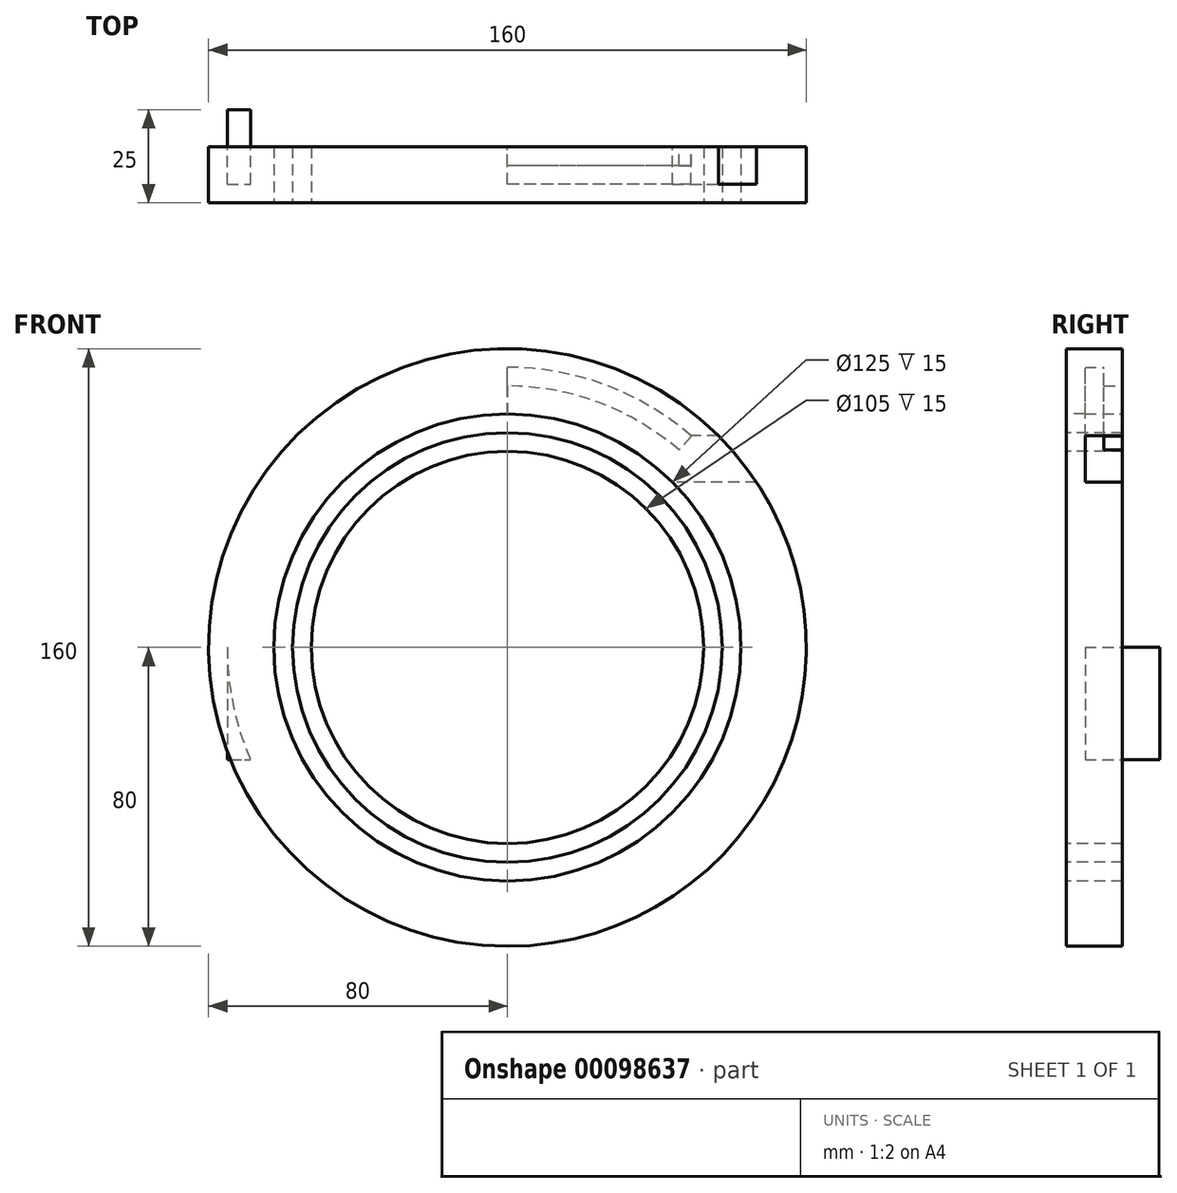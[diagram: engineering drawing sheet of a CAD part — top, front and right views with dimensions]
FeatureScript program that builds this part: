
annotation { "Feature Type Name" : "Feature", "Feature Type Description" : "" }
export const myFeature = defineFeature(function(context is Context, id is Id, definition is map)
    precondition{}
    {
        {
            var Q0;
            Q0=qCreatedBy(makeId("Front.planeOp"),FACE);
            var sketch = newSketch(context, id + "F0", { "sketchPlane" : qUnion([Q0])});
            skCircle(sketch, "E0", {"center": v(0, 0) * mm, "radius": 62.5 * mm});
            skCircle(sketch, "E1", {"center": v(0, 0) * mm, "radius": 75 * mm});
            skLineSegment(sketch, "E2", {"start": v(-62.5, 0) * mm, "end": v(-75, 0) * mm});
            skLineSegment(sketch, "E3", {"start": v(0, 0) * mm, "end": v(53.03, 53.03) * mm});
            skLineSegment(sketch, "E4.bottom", {"start": v(-75, 0) * mm, "end": v(-62.5, 0) * mm});
            skLineSegment(sketch, "E4.top", {"start": v(-75, -30) * mm, "end": v(-62.5, -30) * mm});
            skLineSegment(sketch, "E4.left", {"start": v(-75, 0) * mm, "end": v(-75, -30) * mm});
            skLineSegment(sketch, "E4.right", {"start": v(-62.5, 0) * mm, "end": v(-62.5, -30) * mm});
            skLineSegment(sketch, "E5.left", {"start": v(0, 62.5) * mm, "end": v(0, 75) * mm});
            skLineSegment(sketch, "E6.bottom", {"start": v(44.2, 44.2) * mm, "end": v(79.2, 44.2) * mm});
            skLineSegment(sketch, "E6.top", {"start": v(44.2, 56.7) * mm, "end": v(79.2, 56.7) * mm});
            skLineSegment(sketch, "E6.left", {"start": v(44.2, 44.2) * mm, "end": v(44.2, 56.7) * mm});
            skLineSegment(sketch, "E6.right", {"start": v(79.2, 44.2) * mm, "end": v(79.2, 56.7) * mm});
            skSolve(sketch);
        }
        {
            var Q0;
            {var subQ0=sQuery(id+"F0.wireOp",EDGE,"E4.bottom");Q0=makeQuery(id+"F0.imprint","IMPRINT",FACE,{"disambiguationData":[TD([[makeQuery(id+"F0.imprint","IMPRINT",EDGE,{"derivedFrom":subQ0}),-1.0]])]});}
            var Q1;
            {var subQ0=sQuery(id+"F0.wireOp",EDGE,"E4.left");Q1=makeQuery(id+"F0.imprint","IMPRINT",FACE,{"disambiguationData":[TD([[makeQuery(id+"F0.imprint","IMPRINT",EDGE,{"derivedFrom":subQ0}),1.0]])]});}
            var Q2;
            {var subQ0=sQuery(id+"F0.wireOp",EDGE,"E4.bottom");Q2=makeQuery(id+"F0.imprint","IMPRINT",FACE,{"disambiguationData":[TD([[makeQuery(id+"F0.imprint","IMPRINT",EDGE,{"derivedFrom":subQ0}),1.0]])]});}
            var Q3;
            {var subQ0=sQuery(id+"F0.wireOp",EDGE,"E5.left");Q3=makeQuery(id+"F0.imprint","IMPRINT",FACE,{"disambiguationData":[TD([[makeQuery(id+"F0.imprint","IMPRINT",EDGE,{"derivedFrom":subQ0}),-1.0]])]});}
            var Q4;
            {var subQ3=sQuery(id+"F0.wireOp",EDGE,"E3");var subQ5=sQuery(id+"F0.wireOp",EDGE,"E1");var subQ6=makeQuery(id+"F0.imprint","INTERSECT",VERTEX,{"derivedFrom":[subQ5,subQ3]});Q4=makeQuery(id+"F0.imprint","IMPRINT",FACE,{"disambiguationData":[TD([[makeQuery(id+"F0.imprint","IMPRINT",EDGE,{"disambiguationData":[TD([[subQ6,-1.0]])],"derivedFrom":subQ5}),1.0]])]});}
            var Q5;
            {var subQ0=sQuery(id+"F0.wireOp",EDGE,"E5.top");Q5=makeQuery(id+"F0.imprint","IMPRINT",FACE,{"disambiguationData":[TD([[makeQuery(id+"F0.imprint","IMPRINT",EDGE,{"derivedFrom":subQ0}),-1.0]])]});}
            var Q6;
            {var subQ0=sQuery(id+"F0.wireOp",EDGE,"E6.right");Q6=makeQuery(id+"F0.imprint","IMPRINT",FACE,{"disambiguationData":[TD([[makeQuery(id+"F0.imprint","IMPRINT",EDGE,{"derivedFrom":subQ0}),1.0]])]});}
            var Q7;
            {var subQ0=sQuery(id+"F0.wireOp",EDGE,"E3");var subQ1=sQuery(id+"F0.wireOp",EDGE,"E1");var subQ2=makeQuery(id+"F0.imprint","INTERSECT",VERTEX,{"derivedFrom":[subQ1,subQ0]});Q7=makeQuery(id+"F0.imprint","IMPRINT",FACE,{"disambiguationData":[TD([[makeQuery(id+"F0.imprint","IMPRINT",EDGE,{"disambiguationData":[TD([[subQ2,1.0]])],"derivedFrom":subQ1}),1.0]])]});}
            extrude(context, id + "F1", {"entities" : qUnion([Q0, Q1, Q2, Q3, Q4, Q5, Q6, Q7]), "endBound" : BoundingType.SYMMETRIC, "depth" : 20 * mm});
        }
        {
            var Q0;
            Q0=qCreatedBy(makeId("Front.planeOp"),FACE);
            var sketch = newSketch(context, id + "F2", { "sketchPlane" : qUnion([Q0])});
            skCircle(sketch, "E7", {"center": v(0, 0) * mm, "radius": 75 * mm});
            skCircle(sketch, "E8", {"center": v(0, 0) * mm, "radius": 70 * mm});
            skLineSegment(sketch, "E9", {"start": v(0, 0) * mm, "end": v(49.2, 56.6) * mm});
            skLineSegment(sketch, "E10", {"start": v(0, 0) * mm, "end": v(-75, 0) * mm});
            skSolve(sketch);
        }
        {
            var Q0;
            {var subQ0=sQuery(id+"F2.wireOp",EDGE,"E9");var subQ1=sQuery(id+"F2.wireOp",EDGE,"E7");var subQ2=makeQuery(id+"F2.imprint","INTERSECT",VERTEX,{"derivedFrom":[subQ1,subQ0]});Q0=makeQuery(id+"F2.imprint","IMPRINT",FACE,{"disambiguationData":[TD([[makeQuery(id+"F2.imprint","IMPRINT",EDGE,{"disambiguationData":[TD([[subQ2,-1.0]])],"derivedFrom":subQ1}),1.0]])]});}
            extrude(context, id + "F3", {"entities" : qUnion([Q0]), "operationType" : NewBodyOperationType.REMOVE, "endBound" : BoundingType.SYMMETRIC, "depth" : 10 * mm});
        }
        {
            var Q0;
            Q0=qCreatedBy(makeId("Front.planeOp"),FACE);
            var sketch = newSketch(context, id + "F4", { "sketchPlane" : qUnion([Q0])});
            skCircle(sketch, "E11", {"center": v(0, 0) * mm, "radius": 57.5 * mm});
            skCircle(sketch, "E12", {"center": v(0, 0) * mm, "radius": 80 * mm});
            skLineSegment(sketch, "E13", {"start": v(0, 0) * mm, "end": v(0, 80) * mm});
            skLineSegment(sketch, "E14", {"start": v(0, 80) * mm, "end": v(0, 0) * mm});
            skLineSegment(sketch, "E15", {"start": v(0, 0) * mm, "end": v(-78.78, 13.9) * mm});
            skSolve(sketch);
        }
        {
            var Q0;
            {var subQ0=sQuery(id+"F4.wireOp",EDGE,"E14");var subQ1=sQuery(id+"F4.wireOp",EDGE,"E11");var subQ2=makeQuery(id+"F4.imprint","INTERSECT",VERTEX,{"derivedFrom":[subQ1,subQ0]});Q0=makeQuery(id+"F4.imprint","IMPRINT",FACE,{"disambiguationData":[TD([[makeQuery(id+"F4.imprint","IMPRINT",EDGE,{"disambiguationData":[TD([[subQ2,-1.0]])],"derivedFrom":subQ1}),-1.0]])]});}
            extrude(context, id + "F5", {"entities" : qUnion([Q0]), "depth" : 15 * mm});
        }
        {
            var Q0;
            Q0=makeQuery(id+"F1.opExtrude","SWEPT_BODY",BODY,{"disambiguationData":[OSD([sQuery(id+"F0.wireOp",EDGE,"E0"),sQuery(id+"F0.wireOp",EDGE,"E1"),sQuery(id+"F0.wireOp",EDGE,"E4.top"),sQuery(id+"F0.wireOp",EDGE,"E4.left"),sQuery(id+"F0.wireOp",EDGE,"E4.right"),sQuery(id+"F0.wireOp",EDGE,"E6.bottom"),sQuery(id+"F0.wireOp",EDGE,"E6.top"),sQuery(id+"F0.wireOp",EDGE,"E6.right")])]});
            var Q1;
            Q1=makeQuery(id+"F5.opExtrude","SWEPT_BODY",BODY,{"disambiguationData":[OSD([sQuery(id+"F4.wireOp",EDGE,"E11"),sQuery(id+"F4.wireOp",EDGE,"E12"),sQuery(id+"F4.wireOp",EDGE,"E14"),sQuery(id+"F4.wireOp",EDGE,"E15")])]});
            booleanBodies(context, id + "F6", {"operationType" : BooleanOperationType.SUBTRACTION, "tools" : qUnion([Q0]), "targets" : qUnion([Q1])});
        }
        {
            var Q0;
            Q0=makeQuery(id+"F5.opExtrude","CAP_FACE",FACE,{"disambiguationData":[OSD([sQuery(id+"F4.wireOp",EDGE,"E11"),sQuery(id+"F4.wireOp",EDGE,"E12"),sQuery(id+"F4.wireOp",EDGE,"E14"),sQuery(id+"F4.wireOp",EDGE,"E15")])],"isStart":false});
            var sketch = newSketch(context, id + "F7", { "sketchPlane" : qUnion([Q0])});
            skCircle(sketch, "E16", {"center": v(0, 0) * mm, "radius": 57.5 * mm});
            skCircle(sketch, "E17", {"center": v(0, 0) * mm, "radius": 52.5 * mm});
            skCircle(sketch, "E18", {"center": v(0, 0) * mm, "radius": 62.5 * mm});
            skLineSegment(sketch, "E19", {"start": v(0, 0) * mm, "end": v(-69.28, 40) * mm});
            skLineSegment(sketch, "E20", {"start": v(-69.28, 40) * mm, "end": v(0, 0) * mm});
            skLineSegment(sketch, "E21", {"start": v(0, 0) * mm, "end": v(-27.36, 75.18) * mm});
            skLineSegment(sketch, "E22", {"start": v(0, 0) * mm, "end": v(-17.23, 60.08) * mm});
            skLineSegment(sketch, "E23", {"start": v(-17.23, 60.08) * mm, "end": v(0, 0) * mm});
            skLineSegment(sketch, "E24", {"start": v(0, 0) * mm, "end": v(-12.34, 61.27) * mm});
            skLineSegment(sketch, "E25", {"start": v(-12.34, 61.27) * mm, "end": v(0, 0) * mm});
            skLineSegment(sketch, "E26", {"start": v(0, 0) * mm, "end": v(-8.04, 61.98) * mm});
            skLineSegment(sketch, "E27", {"start": v(-8.04, 61.98) * mm, "end": v(0, 0) * mm});
            skLineSegment(sketch, "E28", {"start": v(0, 0) * mm, "end": v(-51.51, 35.4) * mm});
            skLineSegment(sketch, "E29", {"start": v(-51.51, 35.4) * mm, "end": v(0, 0) * mm});
            skLineSegment(sketch, "E30", {"start": v(-48.92, 38.9) * mm, "end": v(0, 0) * mm});
            skLineSegment(sketch, "E31", {"start": v(-46.08, 42.22) * mm, "end": v(0, 0) * mm});
            skLineSegment(sketch, "E32", {"start": v(0, 0) * mm, "end": v(0, 0) * mm});
            skSolve(sketch);
        }
        {
            var Q0;
            {var subQ0=sQuery(id+"F7.wireOp",EDGE,"E29");var subQ1=sQuery(id+"F7.wireOp",EDGE,"E16");var subQ2=makeQuery(id+"F7.imprint","INTERSECT",VERTEX,{"derivedFrom":[subQ1,subQ0]});Q0=makeQuery(id+"F7.imprint","IMPRINT",FACE,{"disambiguationData":[TD([[makeQuery(id+"F7.imprint","IMPRINT",EDGE,{"disambiguationData":[TD([[subQ2,-1.0]])],"derivedFrom":subQ1}),1.0]])]});}
            var Q1;
            {var subQ0=sQuery(id+"F7.wireOp",EDGE,"E23");var subQ1=sQuery(id+"F7.wireOp",EDGE,"E16");var subQ2=makeQuery(id+"F7.imprint","INTERSECT",VERTEX,{"derivedFrom":[subQ1,subQ0]});Q1=makeQuery(id+"F7.imprint","IMPRINT",FACE,{"disambiguationData":[TD([[makeQuery(id+"F7.imprint","IMPRINT",EDGE,{"disambiguationData":[TD([[subQ2,-1.0]])],"derivedFrom":subQ1}),1.0]])]});}
            var Q2;
            {var subQ0=sQuery(id+"F4.wireOp",EDGE,"E11");var subQ1=sQuery(id+"F4.wireOp",EDGE,"E14");var subQ2=sQuery(id+"F4.wireOp",EDGE,"E15");Q2=makeQuery(id+"F6.opBoolean","SPLIT",FACE,{"disambiguationData":[TD([makeQuery(id+"F1.opExtrude","SWEPT_FACE",FACE,{"disambiguationData":[OSD([sQuery(id+"F0.wireOp",EDGE,"E0")])]})])],"derivedFrom":makeQuery(id+"F5.opExtrude","CAP_FACE",FACE,{"disambiguationData":[OSD([subQ0,sQuery(id+"F4.wireOp",EDGE,"E12"),subQ1,subQ2])],"isStart":true})});}
            extrude(context, id + "F8", {"entities" : qUnion([Q0, Q1]), "operationType" : NewBodyOperationType.ADD, "endBound" : BoundingType.UP_TO_SURFACE, "oppositeDirection" : true, "endBoundEntityFace" : qUnion([Q2]), "depth" : 25 * mm});
        }
        {
            var Q0;
            {var subQ0=sQuery(id+"F7.wireOp",EDGE,"E31");var subQ1=sQuery(id+"F7.wireOp",EDGE,"E16");var subQ2=makeQuery(id+"F7.imprint","INTERSECT",VERTEX,{"derivedFrom":[subQ1,subQ0]});Q0=makeQuery(id+"F7.imprint","IMPRINT",FACE,{"disambiguationData":[TD([[makeQuery(id+"F7.imprint","IMPRINT",EDGE,{"disambiguationData":[TD([[subQ2,-1.0]])],"derivedFrom":subQ1}),-1.0]])]});}
            var Q1;
            {var subQ0=sQuery(id+"F7.wireOp",EDGE,"E27");var subQ1=sQuery(id+"F7.wireOp",EDGE,"E16");var subQ2=makeQuery(id+"F7.imprint","INTERSECT",VERTEX,{"derivedFrom":[subQ1,subQ0]});Q1=makeQuery(id+"F7.imprint","IMPRINT",FACE,{"disambiguationData":[TD([[makeQuery(id+"F7.imprint","IMPRINT",EDGE,{"disambiguationData":[TD([[subQ2,-1.0]])],"derivedFrom":subQ1}),-1.0]])]});}
            extrude(context, id + "F9", {"entities" : qUnion([Q0, Q1]), "operationType" : NewBodyOperationType.REMOVE, "oppositeDirection" : true, "depth" : 25 * mm});
        }
    });
